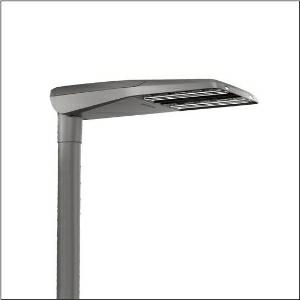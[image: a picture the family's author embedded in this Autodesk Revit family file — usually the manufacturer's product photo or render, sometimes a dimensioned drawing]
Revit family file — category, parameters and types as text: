
# Revit family: streetlight_sl_11_iq_midi___st1_0ab_5xc3n41f08me_2825
name_source: partatom
category: Lighting Fixtures
units: mm (PartAtom-declared; Revit-internal decimal feet)

## family parameters
Cut with Voids When Loaded = No
Host = Face
Light Source = No
Part Type = Normal
Room Calculation Point = No
Round Connector Dimension = Use Diameter
Shared = No

## types (1)
- --- (1 x LED, 15930 lm, 124.7 W, 4000K)
    Apparent Load = 125 VA
    CIE Flux Codes = 29 63 95 100 100
    Color Rendering = 70
    Color Temperature = 4000K
    Default Elevation = 1800 mm
    Description = Streetlight SL 11 iQ midi, mast luminaire, primary light control with 3 zone facetted reflector, of plastic, silver coated, highly specular, primary optical cover: cover, of PMMA, transparent, light distribution: ST1.0aB, light emission: direct distribution, primary light characteristic: asymmetric, installation type: post-top, side-entry, lamps: LED, High Power LED, rated values: 15.930lm | 124,7W | 127,7lm/W (begin service life); end service life: 15.930lm | 132,2W; at 50% lumin. flux: 7.965lm | 57,4W | 138,8lm/W, colour temperature: 4000K, colour rendering: CRI > 70, light colour: 740, light setting 1 begin service life: 100% | 15.930lm | 124,7W | 127,7lm/W | 4.000K, light setting 1 end service life: 132,2W, further light settings possible, control: optimised constant luminous flux control (CLO 2.0), Street-Remote, Desk-Remote (wireless, voltage-free reading and setting of iQ features in the workshop via application-optimized NFC function/RFID function), Light-Fading, Smart-Wire, Night-Set, Lumen-Switch, Temp-Guard, Auto-Match, with cable H07RN-F 3x 1.5mm², mains connection: 230..240V, AC, 50/60Hz, connection cable pre-assembled, cable length: 12,5m, luminaire housing, of diecast aluminium, powder-coated, SITECO metallic grey (DB 702S), please order mast flange separately, inclination adjustable without tools: 0°, 5°, 10°, 15° (post-top) | 0°, -5°, -10°, -15° (side-entry), sealing non-destructively replaceable, multi-level sealing system, length: 780mm, width: 376mm, height: 118mm, mast flange for spigot size: 42mm (side-entry): 5XC10008XM4, 60/48mm (side-entry/post-top): 5XC10108XM2, 76/60mm (side-entry/post-top): 5XC10108XM1, equipment: Power, protection rating (complete): IP66, insulation class (complete): insulation class II (safety insulation), certification: CE, ENEC, ENEC+, VDE, impact resistance: IK10, permissible operating ambient temperature for outdoor applications: -25..+50°C, standard-compliant lighting for roads and squares, Environmental Product Declaration (EPD) tested and certified by an independent institute, packaging unit: 1 piece

Light Distribution: ST1.0aB
    Height = 118 mm
    Lamp = 1 x LED
    Lamp Light Flux = 15930 lm
    Lamp Power = 124.7 W
    Lamp count = 1
    Length = 780 mm
    Luminous efficacy = 128 lm/W
    Manufacturer = Siteco
    ModVariant = No
    Model = 5XC3N41F08ME
    Number of Poles = 1
    OnlyDefault = Yes
    Power Factor = 1
    Product Name = Streetlight SL 11 iQ midi | ST1.0aB
    Product group = mast luminaire | pylon top
    ProductGroupID = 6100
    Protection Class = Protection class II
    Protection Degree = IP 66
    RLX_Detail_Level = 1
    RLX_Emergency_Light_Flux = 0 lm
    RLX_Emergency_Type = 0
    RLX_Emergency_Type_DB = No
    RlxData = <blob elided: 70529 chars, md5=2702a0e1>
    Socket = socket
    Standby Power = 0 W
    System Light Flux = 15930 lm
    System Power = 125 W
    Type Comments = factory setting: luminous flux: 100 % | dim-lin: 254 | 557 mA
    Type Image = l_1005960.jpg
    URL = http://relux.com
    VarID = @adj_091857
    Voltage = 0 V
    Weight = 0.00 kg
    Width = 376 mm

## geometry (parser evidence)
native form markers: Blend x4, Sweep x9
no freeform markers — native parametric forms only
